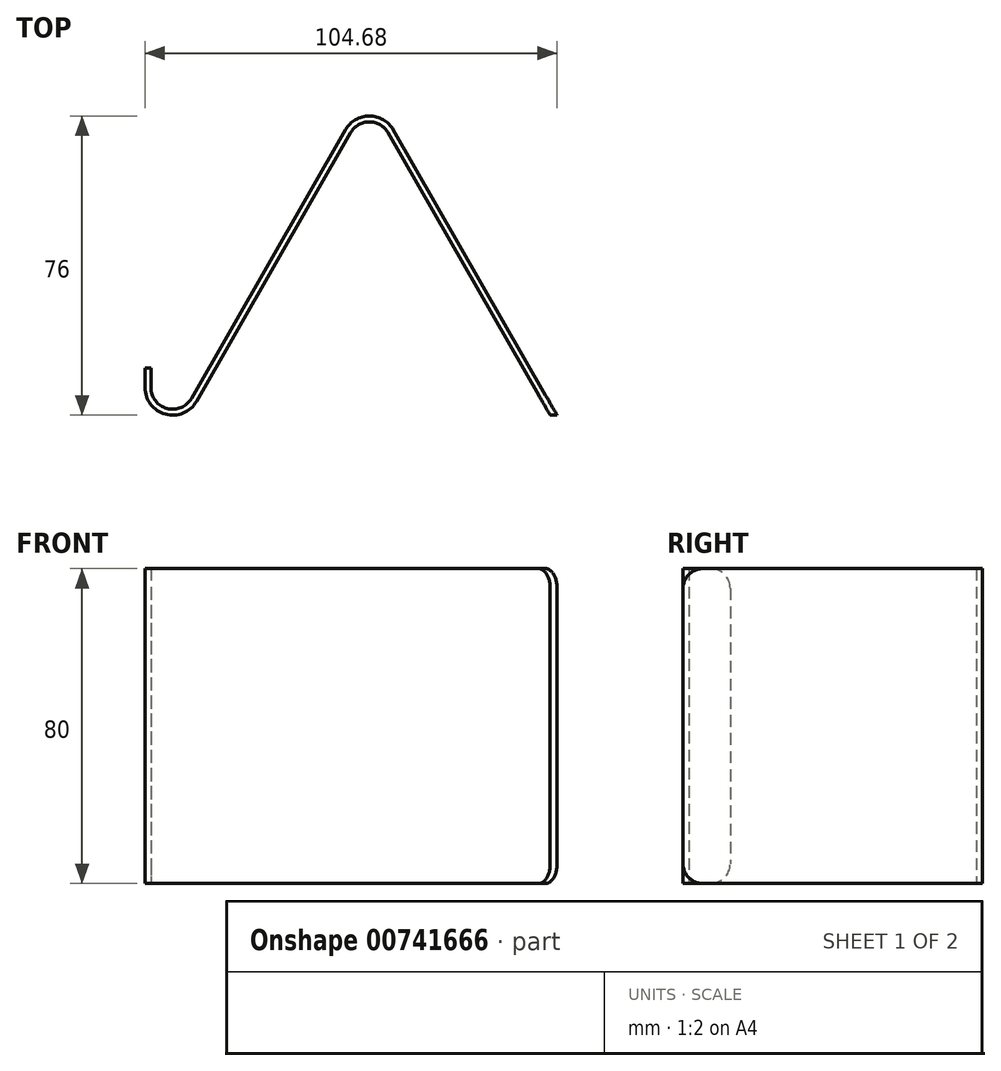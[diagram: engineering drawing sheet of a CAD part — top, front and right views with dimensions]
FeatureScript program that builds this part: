
annotation { "Feature Type Name" : "Feature", "Feature Type Description" : "" }
export const myFeature = defineFeature(function(context is Context, id is Id, definition is map)
    precondition{}
    {
        {
            var Q0;
            Q0=qCreatedBy(makeId("Top.planeOp"),FACE);
            var sketch = newSketch(context, id + "F0", { "sketchPlane" : qUnion([Q0])});
            skArc(sketch, "E0", {"start": v(-7, 0) * mm, "mid": v(-1.8, -6.76) * mm, "end": v(6.07, -3.48) * mm});
            skArc(sketch, "E1", {"start": v(54.77, 64.74) * mm, "mid": v(50, 67.5) * mm, "end": v(45.23, 64.74) * mm});
            skLineSegment(sketch, "E2", {"start": v(6.07, -3.48) * mm, "end": v(45.23, 64.74) * mm});
            skLineSegment(sketch, "E3", {"start": v(50, 62) * mm, "end": v(50, 0) * mm, "construction": true});
            skLineSegment(sketch, "E4.MirrorCS", {"start": v(95.95, -7) * mm, "end": v(54.77, 64.74) * mm});
            skLineSegment(sketch, "E5", {"start": v(0, -7) * mm, "end": v(110.77, -7) * mm, "construction": true});
            skLineSegment(sketch, "E6", {"start": v(-7, 0) * mm, "end": v(-7, 5) * mm});
            skLineSegment(sketch, "E7.0", {"start": v(-5.5, 0) * mm, "end": v(-5.5, 5) * mm});
            skLineSegment(sketch, "E7.1", {"start": v(97.68, -7) * mm, "end": v(56.07, 65.48) * mm});
            skArc(sketch, "E7.2", {"start": v(56.07, 65.48) * mm, "mid": v(50, 69) * mm, "end": v(43.93, 65.48) * mm});
            skLineSegment(sketch, "E7.3", {"start": v(4.77, -2.74) * mm, "end": v(43.93, 65.48) * mm});
            skArc(sketch, "E7.4", {"start": v(-5.5, 0) * mm, "mid": v(-1.42, -5.31) * mm, "end": v(4.77, -2.74) * mm});
            skLineSegment(sketch, "E8", {"start": v(-7, 5) * mm, "end": v(-5.5, 5) * mm});
            skLineSegment(sketch, "E9", {"start": v(95.95, -7) * mm, "end": v(97.68, -7) * mm});
            skSolve(sketch);
        }
        {
            var Q0;
            Q0=qSketchRegion(id+"F0",true);
            extrude(context, id + "F1", {"entities" : qUnion([Q0]), "endBound" : BoundingType.SYMMETRIC, "depth" : 80 * mm});
        }
        {
            var Q0;
            Q0=makeQuery(id+"F1.opExtrude","CAP_EDGE",EDGE,{"disambiguationData":[OSD([sQuery(id+"F0.wireOp",EDGE,"E8")])],"isStart":false});
            var Q1;
            Q1=makeQuery(id+"F1.opExtrude","CAP_EDGE",EDGE,{"disambiguationData":[OSD([sQuery(id+"F0.wireOp",EDGE,"E8")])],"isStart":true});
            var Q2;
            Q2=makeQuery(id+"F1.opExtrude","CAP_EDGE",EDGE,{"disambiguationData":[OSD([sQuery(id+"F0.wireOp",EDGE,"E9")])],"isStart":false});
            var Q3;
            Q3=makeQuery(id+"F1.opExtrude","CAP_EDGE",EDGE,{"disambiguationData":[OSD([sQuery(id+"F0.wireOp",EDGE,"E9")])],"isStart":true});
            fillet(context, id + "F2", {"entities" : qUnion([Q0, Q1, Q2, Q3]), "radius" : 5 * mm, "tangentPropagation" : true, "allowEdgeOverflow" : false});
        }
    });
